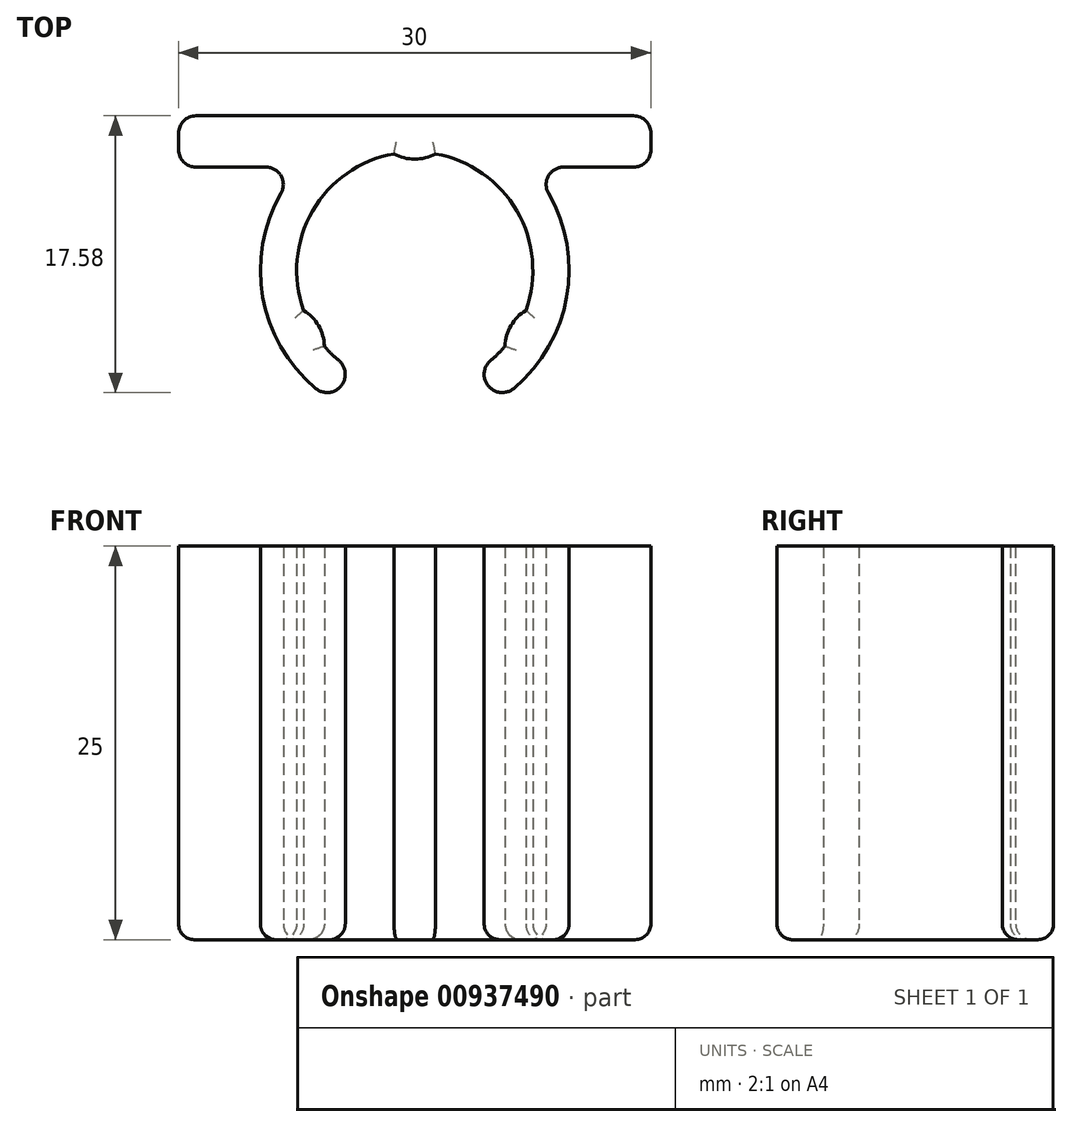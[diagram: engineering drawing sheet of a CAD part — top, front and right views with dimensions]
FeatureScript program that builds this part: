
annotation { "Feature Type Name" : "Feature", "Feature Type Description" : "" }
export const myFeature = defineFeature(function(context is Context, id is Id, definition is map)
    precondition{}
    {
        {
            var Q0;
            Q0=qCreatedBy(makeId("Top.planeOp"),FACE);
            var sketch = newSketch(context, id + "F0", { "sketchPlane" : qUnion([Q0])});
            skArc(sketch, "E0", {"start": v(-5.74, -4.83) * mm, "mid": v(-5.3, -5.3) * mm, "end": v(-4.82, -5.75) * mm});
            skArc(sketch, "E1", {"start": v(6.3, -7.5) * mm, "mid": v(0, 9.8) * mm, "end": v(-6.3, -7.5) * mm});
            skLineSegment(sketch, "E2", {"start": v(0, 0) * mm, "end": v(0, 7.05) * mm, "construction": true});
            skLineSegment(sketch, "E3", {"start": v(0, 0) * mm, "end": v(-6.1, -3.52) * mm, "construction": true});
            skArc(sketch, "E4", {"start": v(7.05, -2.55) * mm, "mid": v(6.1, -3.52) * mm, "end": v(5.74, -4.83) * mm});
            skArc(sketch, "E5", {"start": v(-5.74, -4.83) * mm, "mid": v(-6.1, -3.52) * mm, "end": v(-7.05, -2.55) * mm});
            skArc(sketch, "E6", {"start": v(-1.31, 7.38) * mm, "mid": v(0, 7.05) * mm, "end": v(1.31, 7.38) * mm});
            skArc(sketch, "E7.trimOffspring", {"start": v(-1.31, 7.38) * mm, "mid": v(-6.5, 3.75) * mm, "end": v(-7.05, -2.55) * mm});
            skLineSegment(sketch, "E8", {"start": v(-4.82, -5.75) * mm, "end": v(-5.56, -6.63) * mm, "construction": true});
            skPoint(sketch, "E9", {"position": v(5.56, -6.63) * mm});
            skPoint(sketch, "E10", {"position": v(-5.56, -6.63) * mm});
            skArc(sketch, "E11", {"start": v(4.82, -5.75) * mm, "mid": v(4.68, -7.37) * mm, "end": v(6.3, -7.5) * mm});
            skArc(sketch, "E12", {"start": v(-6.3, -7.5) * mm, "mid": v(-4.68, -7.37) * mm, "end": v(-4.82, -5.75) * mm});
            skArc(sketch, "E13.trimOffspring", {"start": v(4.82, -5.75) * mm, "mid": v(5.3, -5.3) * mm, "end": v(5.74, -4.83) * mm});
            skArc(sketch, "E14.trimOffspring", {"start": v(7.05, -2.55) * mm, "mid": v(6.5, 3.75) * mm, "end": v(1.31, 7.38) * mm});
            skLineSegment(sketch, "E15.trimOffspring", {"start": v(8.49, -4.9) * mm, "end": v(18.18, -10.5) * mm, "construction": true});
            skPoint(sketch, "E16", {"position": v(15, 9.8) * mm});
            skLineSegment(sketch, "E17", {"start": v(15, 9.8) * mm, "end": v(15, 6.54) * mm});
            skLineSegment(sketch, "E18", {"start": v(15, 6.54) * mm, "end": v(7.3, 6.54) * mm});
            skLineSegment(sketch, "E19", {"start": v(15, 9.8) * mm, "end": v(-15, 9.8) * mm});
            skLineSegment(sketch, "E20", {"start": v(-15, 9.8) * mm, "end": v(-15, 6.54) * mm});
            skLineSegment(sketch, "E21", {"start": v(-7.3, 6.54) * mm, "end": v(-15, 6.54) * mm});
            skSolve(sketch);
        }
        {
            var Q0;
            Q0 = qSketchRegion(id + "F0", true);
            extrude(context, id + "F1", {"entities" : qUnion([Q0]), "depth" : 25 * mm, "offsetDistance" : 25 * mm, "symmetric" : true});
        }
        {
            var Q0;
            Q0=makeQuery(id+"F1.opExtrude","SWEPT_EDGE",EDGE,{"disambiguationData":[OSD([sQuery(id+"F0.wireOp",EDGE,"E1"),sQuery(id+"F0.wireOp",EDGE,"E21")])]});
            var Q1;
            Q1=makeQuery(id+"F1.opExtrude","SWEPT_EDGE",EDGE,{"disambiguationData":[OSD([sQuery(id+"F0.wireOp",EDGE,"E20"),sQuery(id+"F0.wireOp",EDGE,"E21")])]});
            var Q2;
            Q2=makeQuery(id+"F1.opExtrude","SWEPT_EDGE",EDGE,{"disambiguationData":[OSD([sQuery(id+"F0.wireOp",EDGE,"E19"),sQuery(id+"F0.wireOp",EDGE,"E20")])]});
            var Q3;
            Q3=makeQuery(id+"F1.opExtrude","SWEPT_EDGE",EDGE,{"disambiguationData":[OSD([sQuery(id+"F0.wireOp",EDGE,"E17"),sQuery(id+"F0.wireOp",EDGE,"E19")])]});
            var Q4;
            Q4=makeQuery(id+"F1.opExtrude","SWEPT_EDGE",EDGE,{"disambiguationData":[OSD([sQuery(id+"F0.wireOp",EDGE,"E17"),sQuery(id+"F0.wireOp",EDGE,"E18")])]});
            var Q5;
            Q5=makeQuery(id+"F1.opExtrude","SWEPT_EDGE",EDGE,{"disambiguationData":[OSD([sQuery(id+"F0.wireOp",EDGE,"E1"),sQuery(id+"F0.wireOp",EDGE,"E18")])]});
            fillet(context, id + "F2", {"entities" : qUnion([Q0, Q1, Q2, Q3, Q4, Q5]), "radius" : 1.1 * mm, "tangentPropagation" : true, "allowEdgeOverflow" : false});
        }
        {
            var Q0;
            Q0=makeQuery(id+"F1.opExtrude","CAP_EDGE",EDGE,{"disambiguationData":[OSD([sQuery(id+"F0.wireOp",EDGE,"E6")])],"isStart":true});
            var Q1;
            Q1=makeQuery(id+"F1.opExtrude","CAP_EDGE",EDGE,{"disambiguationData":[OSD([sQuery(id+"F0.wireOp",EDGE,"E7.trimOffspring")])],"isStart":true});
            var Q2;
            Q2=makeQuery(id+"F1.opExtrude","CAP_EDGE",EDGE,{"disambiguationData":[OSD([sQuery(id+"F0.wireOp",EDGE,"E14.trimOffspring")])],"isStart":true});
            var Q3;
            Q3=makeQuery(id+"F1.opExtrude","CAP_EDGE",EDGE,{"disambiguationData":[OSD([sQuery(id+"F0.wireOp",EDGE,"E4")])],"isStart":true});
            var Q4;
            Q4=makeQuery(id+"F1.opExtrude","CAP_EDGE",EDGE,{"disambiguationData":[OSD([sQuery(id+"F0.wireOp",EDGE,"E13.trimOffspring")])],"isStart":true});
            var Q5;
            Q5=makeQuery(id+"F1.opExtrude","CAP_EDGE",EDGE,{"disambiguationData":[OSD([sQuery(id+"F0.wireOp",EDGE,"E5")])],"isStart":true});
            fillet(context, id + "F3", {"entities" : qUnion([Q0, Q1, Q2, Q3, Q4, Q5]), "radius" : 1 * mm, "tangentPropagation" : true, "allowEdgeOverflow" : false});
        }
    });
